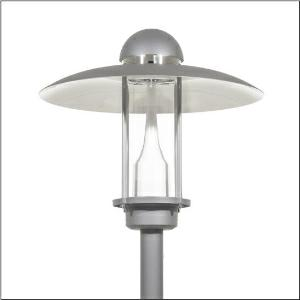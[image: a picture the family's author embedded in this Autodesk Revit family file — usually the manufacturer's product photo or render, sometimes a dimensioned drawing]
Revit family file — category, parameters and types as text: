
# Revit family: city-light_elegance_iq___st1_2a_5xa5265ef14h_e69b
name_source: partatom
category: Lighting Fixtures
units: mm (PartAtom-declared; Revit-internal decimal feet)

## family parameters
Cut with Voids When Loaded = No
Host = Face
Light Source = No
Part Type = Normal
Room Calculation Point = No
Round Connector Dimension = Use Diameter
Shared = No

## types (1)
- --- (1 x LED, 1470 lm, 10.5 W, 3000K)
    Apparent Load = 11 VA
    CIE Flux Codes = 22 62 94 98 100
    Color Rendering = 70
    Color Temperature = 3000K
    Default Elevation = 1800 mm
    Description = City-Light Elegance iQ, mast luminaire, Module 540 iQ-SR, primary light control with 3 zone facetted reflector, of plastic, silver coated, highly specular, structured, primary optical cover: cover, of PMMA, transparent, light distribution: ST1.2a, light emission: direct distribution, primary light characteristic: asymmetric, installation type: post-top, LED, High Power LED, rated luminous flux: 1.470lm, luminous efficacy: 140lm/W, light colour: 730, colour temperature: 3000K, control gear: ECG iQ, control: Auto-Match, Temp-Guard, Lumen-Switch, Night-Set, Smart-Wire, Light-Fading, Desk-Remote (wireless, voltage-free reading and setting of iQ features in the workshop via application-optimized NFC function/RFID function), optimised constant luminous flux control (CLO 2.0), Street-Remote, presetting dimming logarithmic, with terminal, 6-pole, max. 2.5mm², mains connection: 230..240V, AC, 50/60Hz, start of lifetime: 11W, end of service life: 11W, reduction: 5W, luminaire housing, upper part, of aluminium, coated, Siteco® metallic grey (DB 702S), diameter: 750mm, height: 675mm, spigot size: d x l = 76 x 70mm (post-top) | with reducer (optional accessory) 60 x 70mm, post-top mast mounting element, of diecast aluminium, coated, Siteco® metallic grey (DB 702S), Module 540 iQ-SR, traffic white (RAL 9016), equipment: standard, protection rating (complete): IP65, insulation class (complete): insulation class II (safety insulation), certification: CE, ENEC, VDE, packaging unit: 1 piece

Light Distribution: ST1.2a
    Height = 675 mm
    Lamp = 1 x LED
    Lamp Light Flux = 1470 lm
    Lamp Power = 10.5 W
    Lamp count = 1
    Length = 750 mm
    Luminous efficacy = 140 lm/W
    Manufacturer = Siteco
    ModVariant = No
    Model = 5XA5265EF14H
    Number of Poles = 1
    OnlyDefault = Yes
    Power Factor = 1
    Product Name = City-Light Elegance iQ | ST1.2a
    Product group = mast luminaire | pylon top
    ProductGroupID = 6100
    Protection Class = Protection class II
    Protection Degree = IP 65
    RLX_Detail_Level = 1
    RLX_Emergency_Light_Flux = 0 lm
    RLX_Emergency_Type = 0
    RLX_Emergency_Type_DB = No
    RlxData = <blob elided: 99865 chars, md5=86fc1701>
    Socket = socket
    Standby Power = 0 W
    System Light Flux = 1470 lm
    System Power = 11 W
    Type Comments = factory setting: luminous flux: 100 % | dim-lin: 254 | 419 mA
    Type Image = l_1006912.jpg
    URL = http://relux.com
    VarID = @adj_110031
    Voltage = 0 V
    Weight = 0.00 kg
    Width = 0 mm  [stored 0 ft]

note: [stored X ft] marks values corroborated as IEEE doubles in the binary element streams (Revit-internal decimal feet)

## geometry (parser evidence)
native form markers: Blend x4, Sweep x8
no freeform markers — native parametric forms only
